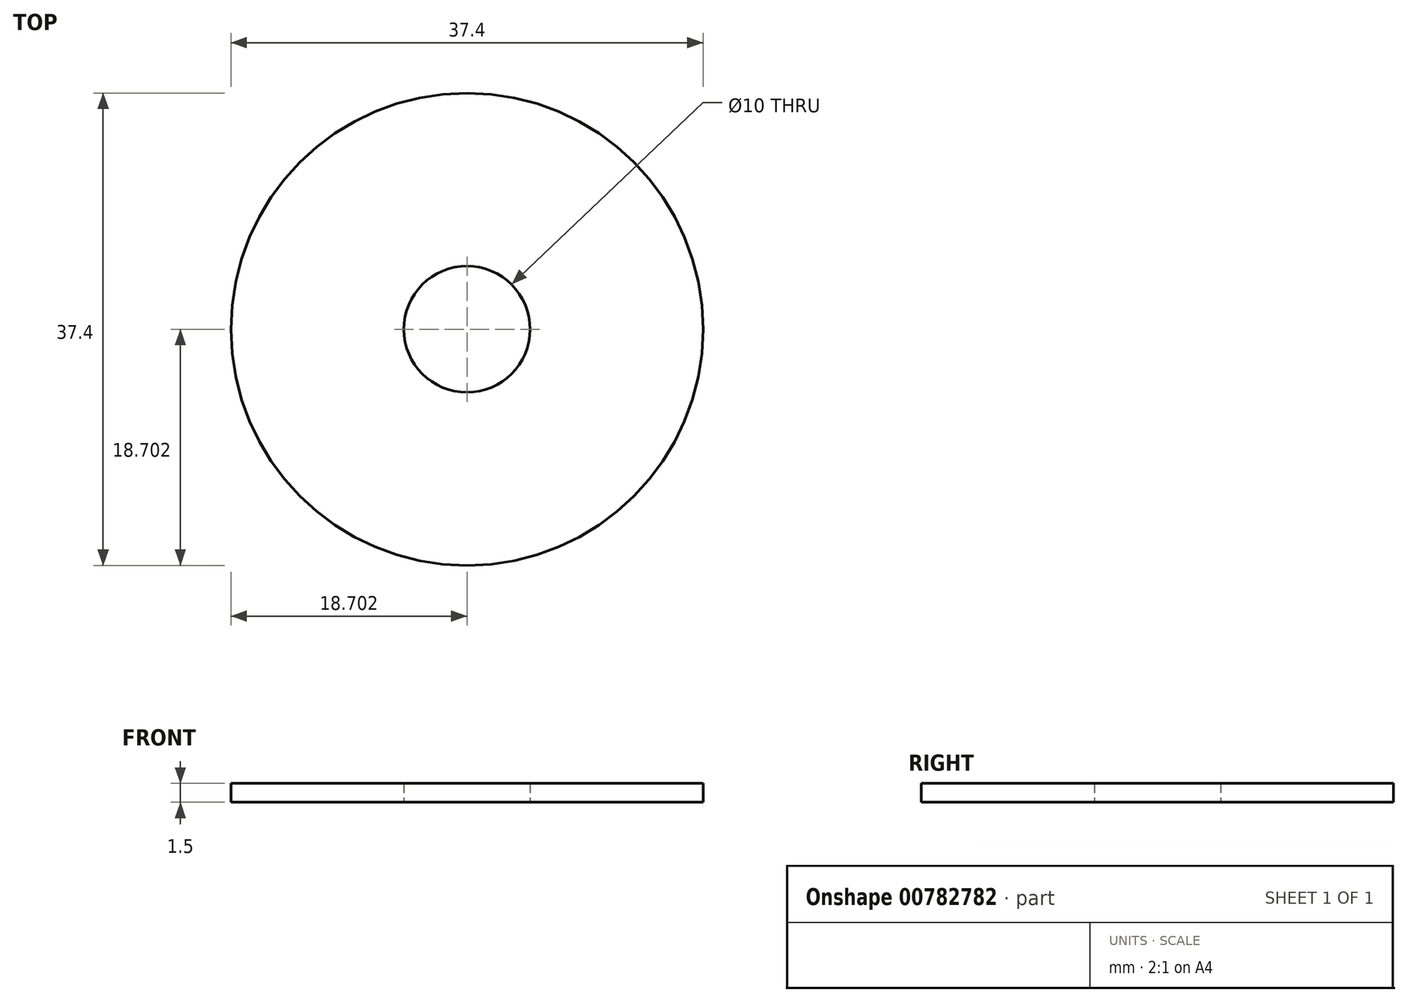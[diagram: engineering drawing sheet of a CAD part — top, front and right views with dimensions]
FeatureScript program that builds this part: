
annotation { "Feature Type Name" : "Feature", "Feature Type Description" : "" }
export const myFeature = defineFeature(function(context is Context, id is Id, definition is map)
    precondition{}
    {
        {
            var Q0;
            Q0=qCreatedBy(makeId("Top.planeOp"),FACE);
            var sketch = newSketch(context, id + "F0", { "sketchPlane" : qUnion([Q0])});
            skCircle(sketch, "E0", {"center": v(-14.38, 6.67) * mm, "radius": 5 * mm});
            skCircle(sketch, "E1", {"center": v(-14.38, 6.67) * mm, "radius": 18.7 * mm});
            skSolve(sketch);
        }
        {
            var Q0;
            Q0 = qSketchRegion(id + "F0", true);
            extrude(context, id + "F1", {"entities" : qUnion([Q0]), "depth" : 1.5 * mm, "offsetDistance" : 25 * mm});
        }
    });
